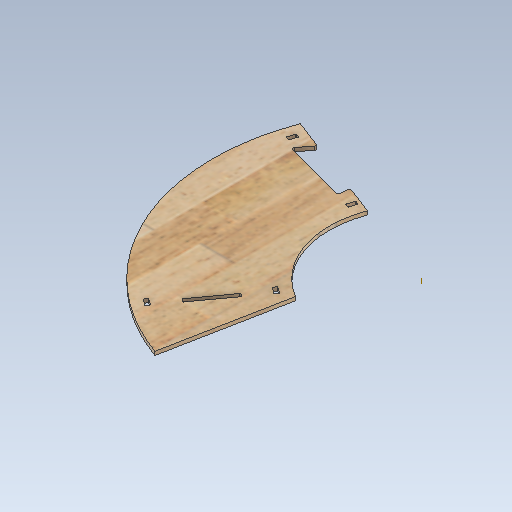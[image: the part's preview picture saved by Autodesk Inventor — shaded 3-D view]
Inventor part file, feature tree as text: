
AUTODESK INVENTOR PART (.ipt)
format: ipt  version: 2020 (Build 240168000, 168)  size: 453,120 bytes
history: native  units: mm
features: extrude x5, sketch x4, pattern_circular x3, mirror x1
ambient origin geometry x8: Origin, YZ Plane, XZ Plane, XY Plane, X Axis, Y Axis, Z Axis, Center Point
bodies: Body1 (feature_tree)
feature tree (13):
  extrude  "Extrusion3"  Depth=6.5mm
  extrude  "Extrusion4"  Depth=2.666667mm
  extrude  "Extrusion5"  Depth=1.333333mm
  sketch  "Sketch5"  dims[d32=1.333333mm d33=1.333333mm]
  extrude  "Extrusion7"  Depth=145.0mm
  pattern_circular  "Circular Pattern2"  Angle=90.0deg  [1 undecoded]
  pattern_circular  "Circular Pattern3"  [2 undecoded]
  mirror  "Mirror3"
  pattern_circular  "Circular Pattern4"  Angle=90.0deg  [1 undecoded]
  extrude  "Extrusion10"  Depth=145.0mm
  sketch  "Sketch2"  dims[d15=6.0mm d16=0.0mm d21=6.5mm]
  sketch  "Sketch3"  dims[d24=2.666667mm d25=2.666667mm]
  sketch  "Sketch6"  dims[d38=0.0mm d39=0.0mm d40=3.25mm d41=90.0deg d42=3.25mm d43=90.0deg d52=4.363323mm d54=10.0mm d55=0.0mm d60=0.872665mm d61=12.566371mm d62=13.439035mm d63=2.666667mm d64=0.523599mm d66=0.523599mm d67=2.666667mm d68=2.666667mm d70=12.566371mm d71=12.566371mm d84=300.14mm d85=682.72mm d86=491.43mm d87=150.07mm d88=341.36mm d89=4.363323mm d90=1.919862mm d91=1.919862mm d94=300.14mm d95=682.72mm d104=6.5mm d105=12.0mm d108=1.333333mm d109=1.333333mm d110=1.333333mm d111=1.333333mm d112=0.0mm d113=0.0mm d114=0.0mm d145=20.0mm d146=12.566371mm d149=145.0mm d150=90.0deg d151=90.0deg d152=90.0deg d153=90.0deg d154=20.0mm d155=25.132741mm d157=20.0mm d158=25.132741mm d169=0.0mm d170=0.0mm]
note: 4 required parameter values undecoded (feature->parameter linkage not recoverable at this tier; creation-order binding heuristic only, values carry confidence <= 0.55)
